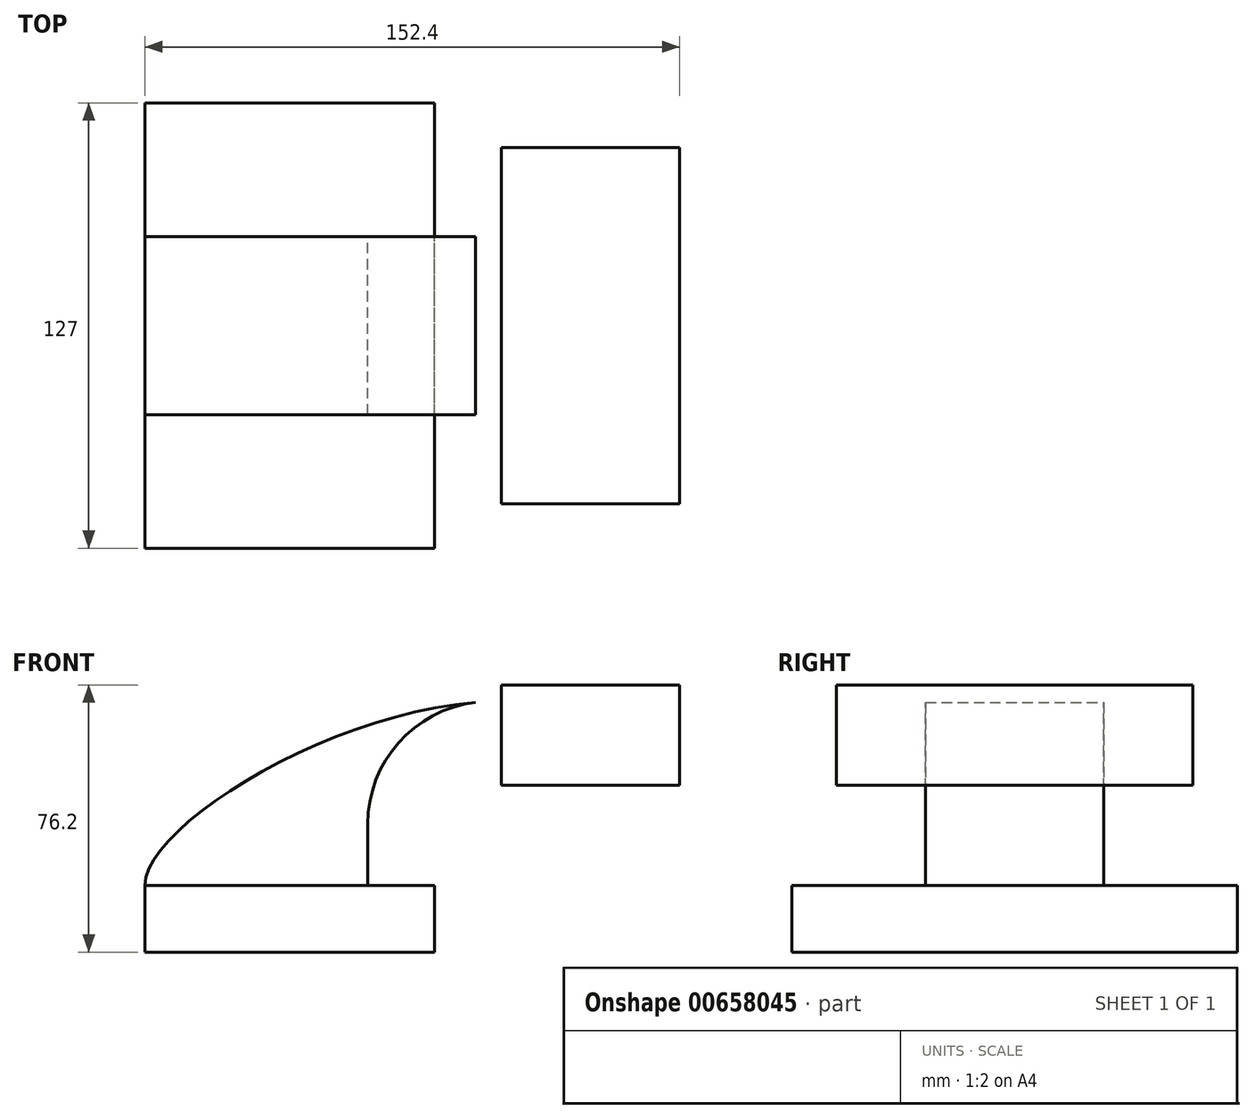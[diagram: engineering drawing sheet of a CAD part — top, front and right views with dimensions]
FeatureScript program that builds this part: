
annotation { "Feature Type Name" : "Feature", "Feature Type Description" : "" }
export const myFeature = defineFeature(function(context is Context, id is Id, definition is map)
    precondition{}
    {
        {
            var Q0;
            Q0=qCreatedBy(makeId("Front.planeOp"),FACE);
            var sketch = newSketch(context, id + "F0", { "sketchPlane" : qUnion([Q0])});
            skLineSegment(sketch, "E0.bottom", {"start": v(41.27, -9.53) * mm, "end": v(-41.28, -9.53) * mm});
            skLineSegment(sketch, "E0.top", {"start": v(41.28, 9.53) * mm, "end": v(-41.28, 9.52) * mm});
            skLineSegment(sketch, "E0.right", {"start": v(-41.28, -9.53) * mm, "end": v(-41.28, 9.52) * mm});
            skPoint(sketch, "E0.middle", {"position": v(0, 0) * mm});
            skPoint(sketch, "E1.middle", {"position": v(41.28, 9.53) * mm});
            skArc(sketch, "E2", {"start": v(41.27, 27) * mm, "mid": v(45.92, 38.23) * mm, "end": v(57.15, 42.88) * mm});
            skLineSegment(sketch, "E3", {"start": v(57.15, 42.88) * mm, "end": v(85.66, 42.88) * mm});
            skLineSegment(sketch, "E4", {"start": v(41.28, 9.53) * mm, "end": v(41.27, -9.53) * mm});
            skLineSegment(sketch, "E5", {"start": v(41.28, 9.53) * mm, "end": v(41.27, 27) * mm});
            skLineSegment(sketch, "E6.bottom", {"start": v(111.12, 38.1) * mm, "end": v(60.32, 38.1) * mm});
            skLineSegment(sketch, "E6.top", {"start": v(111.12, 66.68) * mm, "end": v(60.32, 66.68) * mm});
            skLineSegment(sketch, "E6.left", {"start": v(111.12, 38.1) * mm, "end": v(111.12, 66.68) * mm});
            skLineSegment(sketch, "E6.right", {"start": v(60.32, 38.1) * mm, "end": v(60.32, 66.68) * mm});
            skPoint(sketch, "E6.middle", {"position": v(85.72, 52.39) * mm});
            skLineSegment(sketch, "E7.0", {"start": v(57.15, 61.93) * mm, "end": v(85.66, 61.93) * mm});
            skArc(sketch, "E7.1", {"start": v(22.22, 27) * mm, "mid": v(32.45, 51.7) * mm, "end": v(57.15, 61.93) * mm});
            skLineSegment(sketch, "E7.2", {"start": v(22.22, 9.52) * mm, "end": v(22.22, 27) * mm});
            skLineSegment(sketch, "E8", {"start": v(85.66, 42.88) * mm, "end": v(85.66, 61.93) * mm});
            skFitSpline(sketch, "E9", {"points": [v(-41.28, 9.52) * mm, v(57.15, 61.93) * mm], "startDerivative": vector(0.44, 52.43) * mm, "endDerivative": vector(131.48, 5.05) * mm});
            skSolve(sketch);
        }
        {
            var Q0;
            Q0=makeQuery(id+"F0.imprint","IMPRINT",FACE,{"disambiguationData":[TD([[makeQuery(id+"F0.imprint","IMPRINT",EDGE,{"derivedFrom":sQuery(id+"F0.wireOp",EDGE,"E0.bottom")}),-1.0]])]});
            extrude(context, id + "F1", {"entities" : qUnion([Q0]), "endBound" : BoundingType.SYMMETRIC, "depth" : 127 * mm, "offsetDistance" : 25.4 * mm});
        }
        {
            var Q0;
            {var subQ3=sQuery(id+"F0.wireOp",EDGE,"E7.2");Q0=makeQuery(id+"F0.imprint","IMPRINT",FACE,{"disambiguationData":[TD([[makeQuery(id+"F0.imprint","IMPRINT",EDGE,{"derivedFrom":subQ3}),1.0]])]});}
            extrude(context, id + "F2", {"entities" : qUnion([Q0]), "operationType" : NewBodyOperationType.ADD, "endBound" : BoundingType.SYMMETRIC, "depth" : 50.8 * mm, "offsetDistance" : 25.4 * mm});
        }
        {
            var Q0;
            {var subQ3=sQuery(id+"F0.wireOp",EDGE,"E2");Q0=makeQuery(id+"F0.imprint","IMPRINT",FACE,{"disambiguationData":[TD([[makeQuery(id+"F0.imprint","IMPRINT",EDGE,{"derivedFrom":subQ3}),1.0]])]});}
            var Q1;
            {var subQ0=sQuery(id+"F0.wireOp",EDGE,"E8");Q1=makeQuery(id+"F0.imprint","IMPRINT",FACE,{"disambiguationData":[TD([[makeQuery(id+"F0.imprint","IMPRINT",EDGE,{"derivedFrom":subQ0}),1.0]])]});}
            var Q2;
            {var subQ1=sQuery(id+"F0.wireOp",EDGE,"E6.bottom");Q2=makeQuery(id+"F0.imprint","IMPRINT",FACE,{"disambiguationData":[TD([[makeQuery(id+"F0.imprint","IMPRINT",EDGE,{"derivedFrom":subQ1}),-1.0]])]});}
            extrude(context, id + "F3", {"entities" : qUnion([Q0, Q1, Q2]), "operationType" : NewBodyOperationType.ADD, "endBound" : BoundingType.SYMMETRIC, "depth" : 101.6 * mm, "offsetDistance" : 25.4 * mm});
        }
    });
